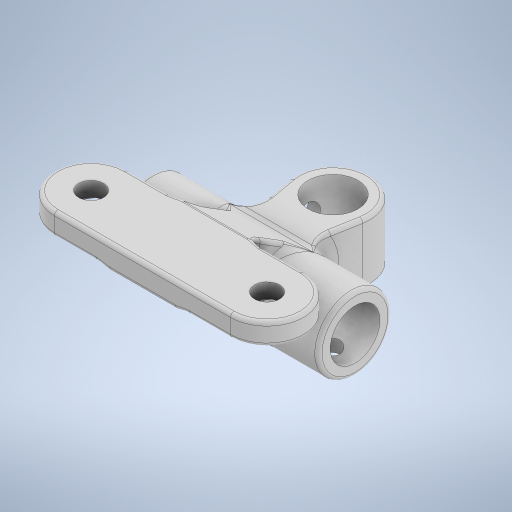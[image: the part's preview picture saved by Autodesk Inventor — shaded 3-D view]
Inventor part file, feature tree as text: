
AUTODESK INVENTOR PART (.ipt)
format: ipt  version: 2024.2 (Build 282272000, 272)  size: 837,120 bytes
history: native  units: mm
features: extrude x11, sketch x10, plane x3, fillet x3, projected_geometry x2
ambient origin geometry x8: Origin, YZ Plane, XZ Plane, XY Plane, X Axis, Y Axis, Z Axis, Center Point
bodies: Solid1 (feature_tree)
feature tree (29):
  extrude  "Extrusion1"  Depth=12.0mm
  extrude  "Extrusion2"  Depth=10.0mm
  sketch  "Sketch3"  dims[d5=3.0mm d6=0.0mm d7=5.7mm]
  extrude  "Extrusion3"  Depth=5.7mm
  extrude  "Extrusion4"  Depth=6.8mm
  plane  "Work Plane1"
  extrude  "Extrusion10"  Depth=10.0mm TaperAngle=0.0deg
  extrude  "Extrusion12"  Depth=6.0mm
  plane  "Work Plane5"
  extrude  "Extrusion16"  Depth=10.0mm
  extrude  "Extrusion17"  Depth=10.0mm TaperAngle=0.0deg
  fillet  "Fillet18"  Radius=10.0mm
  fillet  "Fillet19"  Radius=2.0mm
  fillet  "Fillet20"  Radius=2.8mm
  extrude  "Extrusion13"  Depth=10.0mm
  plane  "Work Plane4"
  extrude  "Extrusion14"  Depth=10.0mm TaperAngle=0.0deg
  extrude  "Extrusion15"  Depth=10.0mm
  sketch  "Sketch1"  dims[d0=24.0mm d1=12.0mm]
  sketch  "Sketch2"  dims[d2=3.4mm d4=10.0mm]
  sketch  "Sketch8"  dims[d8=1.0mm d9=0.0mm d10=6.8mm]
  sketch  "Sketch10"  dims[d11=10.0mm d13=8.0mm d14=0.0mm]
  projected_geometry  "Projected Loop3"
  sketch  "Sketch11"  dims[d15=8.0mm d16=0.0mm d17=6.0mm]
  sketch  "Sketch12"  dims[d41=10.0mm d42=6.8mm]
  sketch  "Sketch13"  dims[d44=8.0mm d45=0.0mm d49=10.0mm d50=0.0mm d52=10.0mm d53=0.0mm d54=2.0mm d55=2.8mm]
  projected_geometry  "Projected Loop4"
  sketch  "Sketch14"  dims[d56=10.0mm d57=0.0mm d61=6.0mm]
  sketch  "Sketch15"  dims[d62=5.25mm d63=2.0mm d64=0.0mm d66=2.0mm d67=6.0mm d68=10.0mm d69=6.0mm d79=10.0mm d80=0.0mm d81=10.0mm d82=0.0mm d83=2.0mm d84=2.0mm d85=0.5mm d86=2.8mm d87=3.0mm d88=3.0mm d28=0.0mm d29=0.0mm d30=0.0mm d31=0.0mm d32=0.0mm d39=0.0mm d40=0.0mm d73=0.0mm d74=0.0mm d75=0.0mm d76=0.0mm d77=0.0mm d78=0.0mm]
